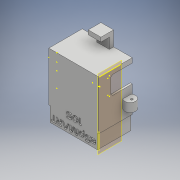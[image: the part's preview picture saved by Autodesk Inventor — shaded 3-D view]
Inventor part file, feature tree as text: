
AUTODESK INVENTOR PART (.ipt)
format: ipt  version: 2018.1 (Build 221171000, 171)  size: 750,080 bytes
history: native  units: mm
features: other x56, sketch x42, extrude x15, split x4, chamfer x4, shell x2, plane x1
ambient origin geometry x8: Origin, YZ Plane, XZ Plane, XY Plane, X Axis, Y Axis, Z Axis, Center Point
bodies: Body1 (feature_tree), Body2 (feature_tree), Body3 (feature_tree)
feature tree (124):
  other  "Sólido1"
  extrude  "Extrusión1"  Depth=17.6mm
  sketch  "Boceto2"  dims[d2=0.9mm d3=0.0mm d6=2.4mm d7=0.0mm d8=0.9mm]
  extrude  "Extrusión2"  Depth=2.4mm TaperAngle=0.0deg
  shell  "Vaciado1"  Thickness=0.9mm
  sketch  "Boceto4"  dims[d11=3.3mm d12=8.0mm d13=0.0mm]
  sketch  "Boceto5"  dims[d14=8.0mm d15=0.0mm d16=8.0mm d17=0.0mm]
  extrude  "Extrusión3"  Depth=2.9mm
  sketch  "Boceto7"  dims[d21=2.0mm]
  sketch  "Boceto8"  dims[d22=24.5mm]
  sketch  "Boceto9"  dims[d23=7.9mm d24=10.4mm d25=0.0mm]
  sketch  "Boceto10"  dims[d26=2.0mm]
  sketch  "Boceto11"  dims[d27=2.0mm]
  sketch  "Boceto12"  dims[d28=2.9mm]
  extrude  "Extrusión4"  Depth=8.0mm TaperAngle=0.0deg
  extrude  "Extrusión5"  Depth=8.0mm TaperAngle=0.0deg
  other  "Engrosado1"
  other  "Engrosado2"
  sketch  "Boceto15"  dims[d31=0.4mm]
  extrude  "Extrusión6"  Depth=2.0mm
  other  "Engrosado3"
  other  "Engrosado4"
  other  "Engrosado5"
  other  "Engrosado6"
  other  "Engrosado7"
  shell  "Vaciado2"  Thickness=2.0mm
  other  "Engrosado8"
  other  "Engrosado9"
  other  "Engrosado10"
  other  "Engrosado11"
  other  "Engrosado12"
  other  "Engrosado13"
  other  "Engrosado14"
  other  "Engrosado15"
  other  "Engrosado16"
  sketch  "Boceto17"  dims[d33=0.4mm]
  plane  "Plano de trabajo1"
  sketch  "Boceto18"  dims[d34=0.4mm]
  sketch  "Boceto19"  dims[d35=0.4mm]
  other  "Forma1"
  split  "Dividir1"
  other  "Engrosado17"
  other  "Engrosado18"
  other  "Engrosado19"
  other  "Engrosado20"
  other  "Engrosado21"
  other  "Suprimir cara1"
  other  "Combinar1"
  other  "Engrosado22"
  other  "Engrosado23"
  chamfer  "Chaflán1"  Distance=10.4mm
  chamfer  "Chaflán2"  Distance=0.1mm
  sketch  "Boceto20"  dims[d36=0.9mm]
  sketch  "Boceto21"  dims[d37=0.4mm]
  other  "Reemplazar cara1"
  other  "Reemplazar cara2"
  other  "Engrosado24"
  other  "Engrosado25"
  other  "Engrosado26"
  chamfer  "Chaflán3"  Distance=0.1mm
  chamfer  "Chaflán4"  Distance=0.2mm
  sketch  "Boceto22"  dims[d38=0.4mm]
  sketch  "Boceto23"  dims[d39=0.4mm]
  sketch  "Boceto24"  dims[d40=0.4mm]
  sketch  "Boceto25"  dims[d41=0.9mm]
  other  "Repujado2"
  other  "Engrosado27"
  extrude  "Extrusión8"  Depth=0.2mm
  other  "Engrosado29"
  extrude  "Extrusión10"  Depth=0.9mm
  split  "Dividir2"
  other  "Engrosado30"
  sketch  "Boceto33"  dims[d44=1.5mm]
  extrude  "Extrusión12"  Depth=0.9mm
  extrude  "Extrusión13"  Depth=4.0mm
  other  "Engrosado31"
  sketch  "Boceto37"  dims[d47=0.6mm]
  other  "Engrosado32"
  other  "Engrosado33"
  sketch  "Boceto38"  dims[d48=0.6mm]
  other  "Engrosado34"
  other  "Engrosado35"
  sketch  "Boceto39"  dims[d49=0.2mm]
  sketch  "Boceto40"  dims[d50=0.2mm]
  other  "Engrosado36"
  sketch  "Boceto41"  dims[d51=0.6mm]
  extrude  "Extrusión14"  Depth=4.0mm
  split  "Dividir3"
  other  "Engrosado37"
  split  "Dividir4"
  other  "Engrosado38"
  other  "Engrosado39"
  other  "Engrosado40"
  other  "Engrosado41"
  other  "Engrosado42"
  other  "Engrosado43"
  sketch  "Boceto45"  dims[d58=0.9mm]
  extrude  "Extrusión17"  Depth=4.0mm
  other  "Engrosado44"
  other  "Engrosado45"
  other  "Engrosado46"
  extrude  "Extrusión19"  Depth=4.0mm
  extrude  "Extrusión20"  Depth=0.8mm TaperAngle=45.0deg
  extrude  "Extrusión21"  Depth=0.8mm TaperAngle=45.0deg
  other  "Engrosado47"
  other  "Engrosado48"
  sketch  "Boceto1"  dims[d0=16.1mm d1=17.6mm]
  sketch  "Boceto3"  dims[d9=3.3mm d10=2.9mm]
  sketch  "Boceto6"  dims[d18=2.0mm d19=2.0mm d20=2.0mm]
  sketch  "Boceto13"  dims[d29=2.9mm]
  sketch  "Boceto14"  dims[d30=0.4mm]
  sketch  "Boceto16"  dims[d32=0.4mm]
  other  "Sólido2"
  sketch  "Boceto30"  dims[d42=0.9mm]
  sketch  "Boceto31"  dims[d43=1.5mm]
  sketch  "Boceto34"  dims[d45=0.8mm]
  sketch  "Boceto36"  dims[d46=0.8mm]
  sketch  "Boceto42"  dims[d52=0.6mm]
  sketch  "Boceto43"  dims[d53=0.6mm]
  sketch  "Boceto44"  dims[d54=0.6mm]
  sketch  "Boceto47"  dims[d59=0.9mm]
  sketch  "Boceto49"  dims[d60=0.8mm]
  sketch  "Boceto50"  dims[d61=0.8mm d62=0.1mm d63=0.1mm d64=0.2mm d65=0.2mm d66=0.9mm d67=0.9mm d68=1.0mm d69=1.0mm d70=1.0mm d71=1.0mm d72=0.8mm d73=2.0mm d74=45.0deg d75=0.8mm d76=2.0mm d77=45.0deg d78=1.5mm d79=1.5mm d80=0.3mm d81=0.3mm d82=0.3mm d83=0.3mm d84=0.8mm d85=2.0mm d86=45.0deg d87=0.8mm d88=2.0mm d89=45.0deg d92=0.7mm d93=0.0mm d94=4.25mm d95=4.25mm d105=11.6mm d106=0.0mm d107=7.3mm d108=7.3mm d114=11.6mm d115=0.0mm d116=7.3mm d117=7.3mm d121=1.0mm d122=4.3mm d123=0.0mm d124=1.0mm d125=4.3mm d126=0.0mm d127=1.2mm d128=1.2mm d129=7.3mm d130=7.3mm d131=7.3mm d132=7.3mm d133=1.3mm d134=7.3mm d135=7.3mm d136=7.3mm d137=7.3mm d138=7.3mm d139=7.3mm d140=2.5mm d141=8.7mm d142=0.0mm d143=4.4mm d144=4.4mm d145=1.0mm d146=4.4mm d147=4.4mm d148=0.1mm d149=0.1mm d150=0.1mm d151=0.1mm d152=0.1mm d153=0.1mm d154=0.1mm d155=0.1mm d156=0.2mm d157=0.2mm d158=11.25mm d159=3.0mm d160=3.0mm d167=11.85mm d168=3.0mm d169=3.0mm d171=7.0mm d172=0.0mm d176=0.1mm d177=0.1mm d178=0.1mm d179=0.1mm d180=0.1mm d181=0.1mm d182=2.0mm d183=2.0mm d184=4.0mm d185=0.0mm d186=2.0mm d187=7.0mm d188=0.0mm d189=2.0mm d190=4.0mm d191=0.0mm d192=0.1mm d193=0.1mm d194=0.1mm d195=0.1mm]
  other  "Sup1"
